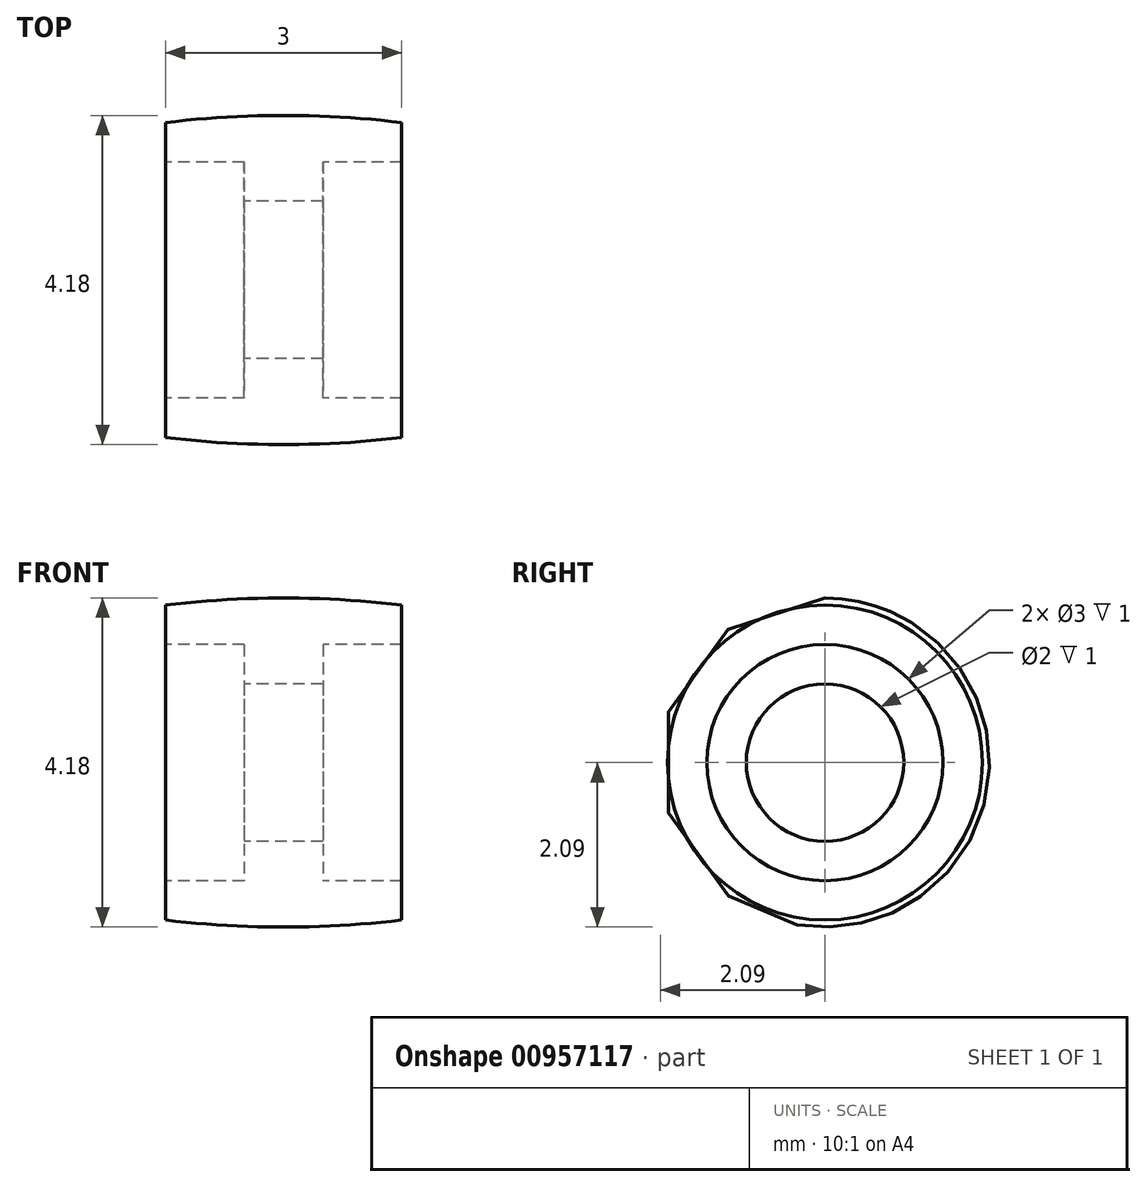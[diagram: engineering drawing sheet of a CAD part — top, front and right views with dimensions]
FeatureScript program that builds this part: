
annotation { "Feature Type Name" : "Feature", "Feature Type Description" : "" }
export const myFeature = defineFeature(function(context is Context, id is Id, definition is map)
    precondition{}
    {
        {
            var Q0;
            Q0=qCreatedBy(makeId("Front.planeOp"),FACE);
            var sketch = newSketch(context, id + "F0", { "sketchPlane" : qUnion([Q0])});
            skArc(sketch, "E0", {"start": v(1.5, 12.4) * mm, "mid": v(0, 12.5) * mm, "end": v(-1.5, 12.4) * mm});
            skLineSegment(sketch, "E1", {"start": v(-1.5, 12.4) * mm, "end": v(-1.5, 11.9) * mm});
            skLineSegment(sketch, "E2", {"start": v(-1.5, 11.9) * mm, "end": v(-0.5, 11.9) * mm});
            skLineSegment(sketch, "E3", {"start": v(-0.5, 11.9) * mm, "end": v(-0.5, 11.4) * mm});
            skLineSegment(sketch, "E4", {"start": v(-0.5, 11.4) * mm, "end": v(0, 11.4) * mm});
            skLineSegment(sketch, "E5", {"start": v(0, 0) * mm, "end": v(0, 12.13) * mm, "construction": true});
            skLineSegment(sketch, "E6.MirrorCS", {"start": v(1.5, 12.4) * mm, "end": v(1.5, 11.9) * mm});
            skLineSegment(sketch, "E7.MirrorCS", {"start": v(1.5, 11.9) * mm, "end": v(0.5, 11.9) * mm});
            skLineSegment(sketch, "E8.MirrorCS", {"start": v(0.5, 11.9) * mm, "end": v(0.5, 11.4) * mm});
            skLineSegment(sketch, "E9.MirrorCS", {"start": v(0.5, 11.4) * mm, "end": v(0, 11.4) * mm});
            skLineSegment(sketch, "E10", {"start": v(-9.68, 10.4) * mm, "end": v(9.57, 10.4) * mm, "construction": true});
            skCircle(sketch, "E11", {"center": v(0, 0) * mm, "radius": 12.5 * mm, "construction": true});
            skSolve(sketch);
        }
        {
            var Q0;
            Q0=makeQuery(id+"F0.imprint","IMPRINT",FACE,{"disambiguationData":[TD([[makeQuery(id+"F0.imprint","IMPRINT",EDGE,{"derivedFrom":sQuery(id+"F0.wireOp",EDGE,"E0")}),1.0]])]});
            var Q1;
            Q1=sQuery(id+"F0.wireOp",EDGE,"E10");
            revolve(context, id + "F1", {"surfaceOperationType" : NewSurfaceOperationType.NEW, "entities" : qUnion([Q0]), "axis" : qUnion([Q1]), "revolveType" : RevolveType.FULL});
        }
    });
